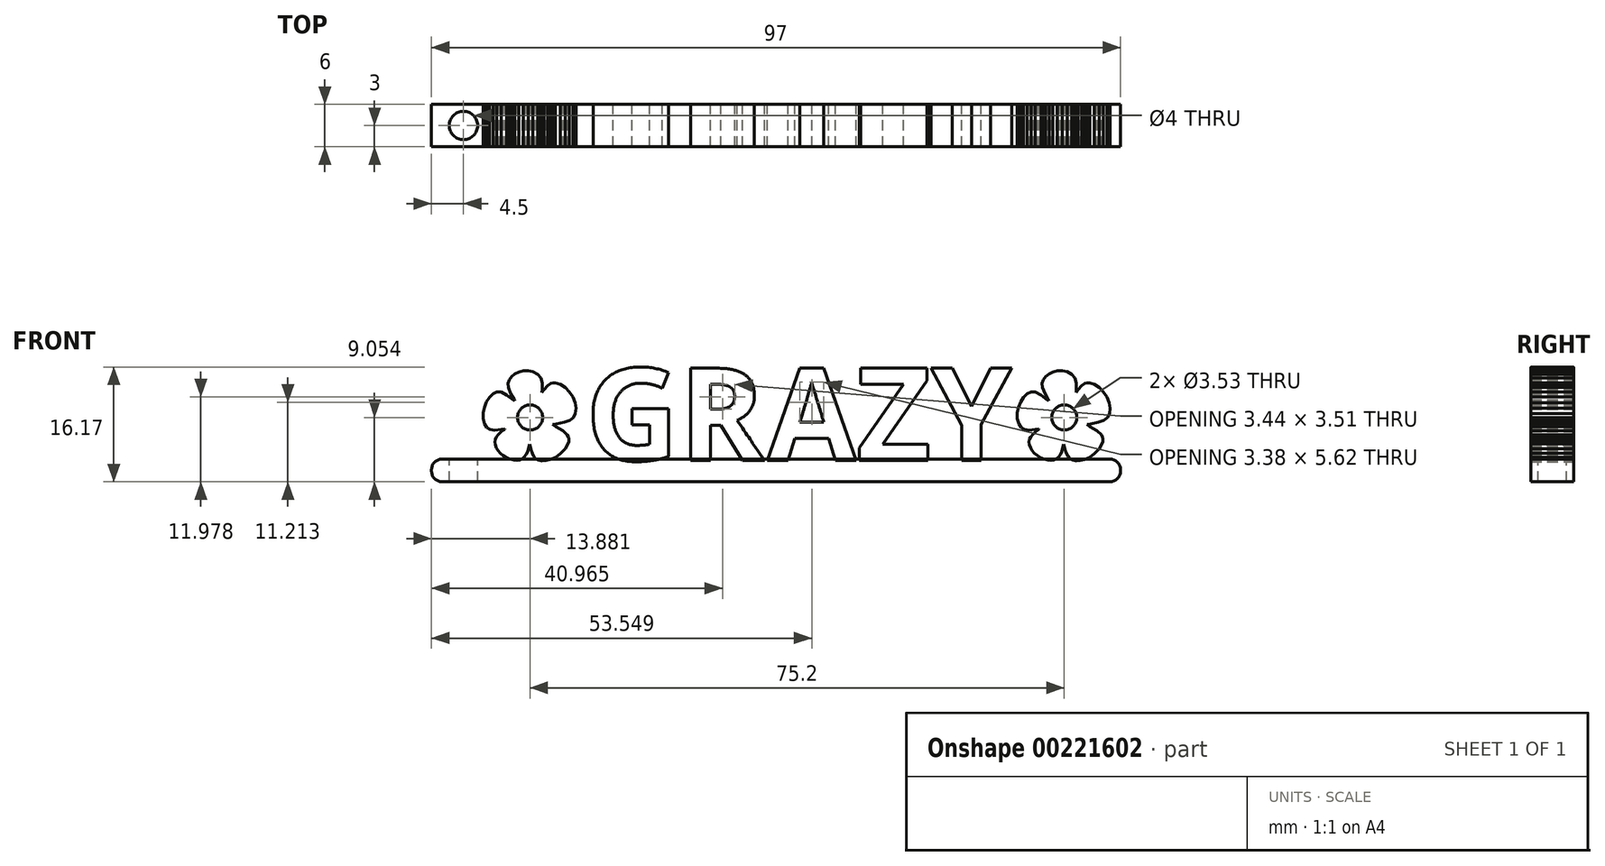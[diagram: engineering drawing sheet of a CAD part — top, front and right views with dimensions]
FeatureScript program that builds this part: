
annotation { "Feature Type Name" : "Feature", "Feature Type Description" : "" }
export const myFeature = defineFeature(function(context is Context, id is Id, definition is map)
    precondition{}
    {
        {
            var Q0;
            Q0=qCreatedBy(makeId("Front.planeOp"),FACE);
            var sketch = newSketch(context, id + "F0", { "sketchPlane" : qUnion([Q0])});
            skText(sketch, "E0", { "text": "   GRAZY", "fontName": "OpenSans-Bold.ttf"});
            skLineSegment(sketch, "E1.0.0", {"start": v(-9.3, 0.1) * mm, "end": v(-8.53, 0.46) * mm});
            skLineSegment(sketch, "E1.0.1", {"start": v(-8.53, 0.46) * mm, "end": v(-7.79, 1.02) * mm});
            skLineSegment(sketch, "E1.0.2", {"start": v(-7.79, 1.02) * mm, "end": v(-7.18, 1.67) * mm});
            skLineSegment(sketch, "E1.0.3", {"start": v(-7.18, 1.67) * mm, "end": v(-6.78, 2.35) * mm});
            skLineSegment(sketch, "E1.0.4", {"start": v(-6.78, 2.35) * mm, "end": v(-6.68, 2.7) * mm});
            skLineSegment(sketch, "E1.0.5", {"start": v(-6.68, 2.7) * mm, "end": v(-6.67, 3.02) * mm});
            skLineSegment(sketch, "E1.0.6", {"start": v(-6.67, 3.02) * mm, "end": v(-6.73, 3.33) * mm});
            skLineSegment(sketch, "E1.0.7", {"start": v(-6.73, 3.33) * mm, "end": v(-6.89, 3.62) * mm});
            skLineSegment(sketch, "E1.0.8", {"start": v(-6.89, 3.62) * mm, "end": v(-7.48, 4.2) * mm});
            skLineSegment(sketch, "E1.0.9", {"start": v(-7.48, 4.2) * mm, "end": v(-8.5, 4.79) * mm});
            skLineSegment(sketch, "E1.0.10", {"start": v(-8.5, 4.79) * mm, "end": v(-8.93, 5.06) * mm});
            skLineSegment(sketch, "E1.0.11", {"start": v(-8.93, 5.06) * mm, "end": v(-8.42, 5.16) * mm});
            skLineSegment(sketch, "E1.0.12", {"start": v(-8.42, 5.16) * mm, "end": v(-7.31, 5.37) * mm});
            skLineSegment(sketch, "E1.0.13", {"start": v(-7.31, 5.37) * mm, "end": v(-6.55, 5.65) * mm});
            skLineSegment(sketch, "E1.0.14", {"start": v(-6.55, 5.65) * mm, "end": v(-6.05, 6.04) * mm});
            skLineSegment(sketch, "E1.0.15", {"start": v(-6.05, 6.04) * mm, "end": v(-5.76, 6.58) * mm});
            skLineSegment(sketch, "E1.0.16", {"start": v(-5.76, 6.58) * mm, "end": v(-5.64, 7.33) * mm});
            skLineSegment(sketch, "E1.0.17", {"start": v(-5.64, 7.33) * mm, "end": v(-5.78, 8.14) * mm});
            skLineSegment(sketch, "E1.0.18", {"start": v(-5.78, 8.14) * mm, "end": v(-6.1, 8.93) * mm});
            skLineSegment(sketch, "E1.0.19", {"start": v(-6.1, 8.93) * mm, "end": v(-6.6, 9.67) * mm});
            skLineSegment(sketch, "E1.0.20", {"start": v(-6.6, 9.67) * mm, "end": v(-7.2, 10.28) * mm});
            skLineSegment(sketch, "E1.0.21", {"start": v(-7.2, 10.28) * mm, "end": v(-7.86, 10.72) * mm});
            skLineSegment(sketch, "E1.0.22", {"start": v(-7.86, 10.72) * mm, "end": v(-8.55, 10.93) * mm});
            skLineSegment(sketch, "E1.0.23", {"start": v(-8.55, 10.93) * mm, "end": v(-8.88, 10.93) * mm});
            skLineSegment(sketch, "E1.0.24", {"start": v(-8.88, 10.93) * mm, "end": v(-9.2, 10.85) * mm});
            skLineSegment(sketch, "E1.0.25", {"start": v(-9.2, 10.85) * mm, "end": v(-9.65, 10.56) * mm});
            skLineSegment(sketch, "E1.0.26", {"start": v(-9.65, 10.56) * mm, "end": v(-10.14, 9.98) * mm});
            skLineSegment(sketch, "E1.0.27", {"start": v(-10.14, 9.98) * mm, "end": v(-10.45, 9.58) * mm});
            skLineSegment(sketch, "E1.0.28", {"start": v(-10.45, 9.58) * mm, "end": v(-10.4, 10.03) * mm});
            skLineSegment(sketch, "E1.0.29", {"start": v(-10.4, 10.03) * mm, "end": v(-10.4, 10.93) * mm});
            skLineSegment(sketch, "E1.0.30", {"start": v(-10.4, 10.93) * mm, "end": v(-10.6, 11.63) * mm});
            skLineSegment(sketch, "E1.0.31", {"start": v(-10.6, 11.63) * mm, "end": v(-11.04, 12.15) * mm});
            skLineSegment(sketch, "E1.0.32", {"start": v(-11.04, 12.15) * mm, "end": v(-11.71, 12.5) * mm});
            skLineSegment(sketch, "E1.0.33", {"start": v(-11.71, 12.5) * mm, "end": v(-12.4, 12.64) * mm});
            skLineSegment(sketch, "E1.0.34", {"start": v(-12.4, 12.64) * mm, "end": v(-13.07, 12.62) * mm});
            skLineSegment(sketch, "E1.0.35", {"start": v(-13.07, 12.62) * mm, "end": v(-13.7, 12.47) * mm});
            skLineSegment(sketch, "E1.0.36", {"start": v(-13.7, 12.47) * mm, "end": v(-14.26, 12.2) * mm});
            skLineSegment(sketch, "E1.0.37", {"start": v(-14.26, 12.2) * mm, "end": v(-14.72, 11.83) * mm});
            skLineSegment(sketch, "E1.0.38", {"start": v(-14.72, 11.83) * mm, "end": v(-15.05, 11.38) * mm});
            skLineSegment(sketch, "E1.0.39", {"start": v(-15.05, 11.38) * mm, "end": v(-15.22, 10.87) * mm});
            skLineSegment(sketch, "E1.0.40", {"start": v(-15.22, 10.87) * mm, "end": v(-15.2, 10.3) * mm});
            skLineSegment(sketch, "E1.0.41", {"start": v(-15.2, 10.3) * mm, "end": v(-14.83, 9.4) * mm});
            skLineSegment(sketch, "E1.0.42", {"start": v(-14.83, 9.4) * mm, "end": v(-14.35, 8.55) * mm});
            skLineSegment(sketch, "E1.0.43", {"start": v(-14.35, 8.55) * mm, "end": v(-14.3, 8.4) * mm});
            skLineSegment(sketch, "E1.0.44", {"start": v(-14.3, 8.4) * mm, "end": v(-14.48, 8.53) * mm});
            skLineSegment(sketch, "E1.0.45", {"start": v(-14.48, 8.53) * mm, "end": v(-15.4, 9.23) * mm});
            skLineSegment(sketch, "E1.0.46", {"start": v(-15.4, 9.23) * mm, "end": v(-16.22, 9.63) * mm});
            skLineSegment(sketch, "E1.0.47", {"start": v(-16.22, 9.63) * mm, "end": v(-16.8, 9.63) * mm});
            skLineSegment(sketch, "E1.0.48", {"start": v(-16.8, 9.63) * mm, "end": v(-17.36, 9.37) * mm});
            skLineSegment(sketch, "E1.0.49", {"start": v(-17.36, 9.37) * mm, "end": v(-17.85, 8.9) * mm});
            skLineSegment(sketch, "E1.0.50", {"start": v(-17.85, 8.9) * mm, "end": v(-18.26, 8.26) * mm});
            skLineSegment(sketch, "E1.0.51", {"start": v(-18.26, 8.26) * mm, "end": v(-18.56, 7.51) * mm});
            skLineSegment(sketch, "E1.0.52", {"start": v(-18.56, 7.51) * mm, "end": v(-18.72, 6.71) * mm});
            skLineSegment(sketch, "E1.0.53", {"start": v(-18.72, 6.71) * mm, "end": v(-18.72, 5.9) * mm});
            skLineSegment(sketch, "E1.0.54", {"start": v(-18.72, 5.9) * mm, "end": v(-18.52, 5.16) * mm});
            skLineSegment(sketch, "E1.0.55", {"start": v(-18.52, 5.16) * mm, "end": v(-18.2, 4.64) * mm});
            skLineSegment(sketch, "E1.0.56", {"start": v(-18.2, 4.64) * mm, "end": v(-17.75, 4.36) * mm});
            skLineSegment(sketch, "E1.0.57", {"start": v(-17.75, 4.36) * mm, "end": v(-17.1, 4.27) * mm});
            skLineSegment(sketch, "E1.0.58", {"start": v(-17.1, 4.27) * mm, "end": v(-16.21, 4.37) * mm});
            skLineSegment(sketch, "E1.0.59", {"start": v(-16.21, 4.37) * mm, "end": v(-15.7, 4.43) * mm});
            skLineSegment(sketch, "E1.0.60", {"start": v(-15.7, 4.43) * mm, "end": v(-15.67, 4.4) * mm});
            skLineSegment(sketch, "E1.0.61", {"start": v(-15.67, 4.4) * mm, "end": v(-15.78, 4.33) * mm});
            skLineSegment(sketch, "E1.0.62", {"start": v(-15.78, 4.33) * mm, "end": v(-16.17, 4.07) * mm});
            skLineSegment(sketch, "E1.0.63", {"start": v(-16.17, 4.07) * mm, "end": v(-16.55, 3.71) * mm});
            skLineSegment(sketch, "E1.0.64", {"start": v(-16.55, 3.71) * mm, "end": v(-16.87, 3.33) * mm});
            skLineSegment(sketch, "E1.0.65", {"start": v(-16.87, 3.33) * mm, "end": v(-17.04, 3) * mm});
            skLineSegment(sketch, "E1.0.66", {"start": v(-17.04, 3) * mm, "end": v(-17.08, 2.6) * mm});
            skLineSegment(sketch, "E1.0.67", {"start": v(-17.08, 2.6) * mm, "end": v(-17.02, 2.2) * mm});
            skLineSegment(sketch, "E1.0.68", {"start": v(-17.02, 2.2) * mm, "end": v(-16.87, 1.78) * mm});
            skLineSegment(sketch, "E1.0.69", {"start": v(-16.87, 1.78) * mm, "end": v(-16.62, 1.39) * mm});
            skLineSegment(sketch, "E1.0.70", {"start": v(-16.62, 1.39) * mm, "end": v(-16.3, 1.02) * mm});
            skLineSegment(sketch, "E1.0.71", {"start": v(-16.3, 1.02) * mm, "end": v(-15.9, 0.69) * mm});
            skLineSegment(sketch, "E1.0.72", {"start": v(-15.9, 0.69) * mm, "end": v(-15.45, 0.4) * mm});
            skLineSegment(sketch, "E1.0.73", {"start": v(-15.45, 0.4) * mm, "end": v(-14.95, 0.2) * mm});
            skLineSegment(sketch, "E1.0.74", {"start": v(-14.95, 0.2) * mm, "end": v(-14.44, 0.06) * mm});
            skLineSegment(sketch, "E1.0.75", {"start": v(-14.44, 0.06) * mm, "end": v(-13.98, 0.02) * mm});
            skLineSegment(sketch, "E1.0.76", {"start": v(-13.98, 0.02) * mm, "end": v(-13.58, 0.08) * mm});
            skLineSegment(sketch, "E1.0.77", {"start": v(-13.58, 0.08) * mm, "end": v(-13.23, 0.23) * mm});
            skLineSegment(sketch, "E1.0.78", {"start": v(-13.23, 0.23) * mm, "end": v(-12.92, 0.49) * mm});
            skLineSegment(sketch, "E1.0.79", {"start": v(-12.92, 0.49) * mm, "end": v(-12.67, 0.84) * mm});
            skLineSegment(sketch, "E1.0.80", {"start": v(-12.67, 0.84) * mm, "end": v(-12.46, 1.28) * mm});
            skLineSegment(sketch, "E1.0.81", {"start": v(-12.46, 1.28) * mm, "end": v(-12.3, 1.83) * mm});
            skLineSegment(sketch, "E1.0.82", {"start": v(-12.3, 1.83) * mm, "end": v(-12.19, 2.26) * mm});
            skLineSegment(sketch, "E1.0.83", {"start": v(-12.19, 2.26) * mm, "end": v(-12.13, 2.1) * mm});
            skLineSegment(sketch, "E1.0.84", {"start": v(-12.13, 2.1) * mm, "end": v(-12.01, 1.53) * mm});
            skLineSegment(sketch, "E1.0.85", {"start": v(-12.01, 1.53) * mm, "end": v(-11.82, 1) * mm});
            skLineSegment(sketch, "E1.0.86", {"start": v(-11.82, 1) * mm, "end": v(-11.6, 0.55) * mm});
            skLineSegment(sketch, "E1.0.87", {"start": v(-11.6, 0.55) * mm, "end": v(-11.35, 0.26) * mm});
            skLineSegment(sketch, "E1.0.88", {"start": v(-11.35, 0.26) * mm, "end": v(-10.95, 0.05) * mm});
            skLineSegment(sketch, "E1.0.89", {"start": v(-10.95, 0.05) * mm, "end": v(-10.46, -0.04) * mm});
            skLineSegment(sketch, "E1.0.90", {"start": v(-10.46, -0.04) * mm, "end": v(-9.9, -0.03) * mm});
            skLineSegment(sketch, "E1.0.91", {"start": v(-9.9, -0.03) * mm, "end": v(-9.3, 0.1) * mm});
            skCircle(sketch, "E2", {"center": v(-12.12, 6.05) * mm, "radius": 1.77 * mm});
            skCircle(sketch, "E3.1.0.0", {"center": v(63.08, 6.05) * mm, "radius": 1.77 * mm});
            skLineSegment(sketch, "E3.1.0.1", {"start": v(64.75, 9.58) * mm, "end": v(64.8, 10.03) * mm});
            skLineSegment(sketch, "E3.1.0.2", {"start": v(68, 10.28) * mm, "end": v(67.34, 10.72) * mm});
            skLineSegment(sketch, "E3.1.0.3", {"start": v(56.48, 5.9) * mm, "end": v(56.68, 5.16) * mm});
            skLineSegment(sketch, "E3.1.0.4", {"start": v(60.94, 12.2) * mm, "end": v(60.48, 11.83) * mm});
            skLineSegment(sketch, "E3.1.0.5", {"start": v(58.9, 1.02) * mm, "end": v(59.3, 0.69) * mm});
            skLineSegment(sketch, "E3.1.0.6", {"start": v(58.98, 9.63) * mm, "end": v(58.4, 9.63) * mm});
            skLineSegment(sketch, "E3.1.0.7", {"start": v(56.64, 7.51) * mm, "end": v(56.48, 6.71) * mm});
            skLineSegment(sketch, "E3.1.0.8", {"start": v(59.8, 9.23) * mm, "end": v(58.98, 9.63) * mm});
            skLineSegment(sketch, "E3.1.0.9", {"start": v(58.4, 9.63) * mm, "end": v(57.84, 9.37) * mm});
            skLineSegment(sketch, "E3.1.0.10", {"start": v(65.06, 9.98) * mm, "end": v(64.75, 9.58) * mm});
            skLineSegment(sketch, "E3.1.0.11", {"start": v(64.6, 11.63) * mm, "end": v(64.16, 12.15) * mm});
            skLineSegment(sketch, "E3.1.0.12", {"start": v(64.16, 12.15) * mm, "end": v(63.49, 12.5) * mm});
            skLineSegment(sketch, "E3.1.0.13", {"start": v(64.8, 10.93) * mm, "end": v(64.6, 11.63) * mm});
            skLineSegment(sketch, "E3.1.0.14", {"start": v(59.75, 0.4) * mm, "end": v(60.25, 0.2) * mm});
            skLineSegment(sketch, "E3.1.0.15", {"start": v(65.3, -0.03) * mm, "end": v(65.9, 0.1) * mm});
            skLineSegment(sketch, "E3.1.0.16", {"start": v(56.48, 6.71) * mm, "end": v(56.48, 5.9) * mm});
            skLineSegment(sketch, "E3.1.0.17", {"start": v(65.9, 0.1) * mm, "end": v(66.67, 0.46) * mm});
            skLineSegment(sketch, "E3.1.0.18", {"start": v(59.3, 0.69) * mm, "end": v(59.75, 0.4) * mm});
            skLineSegment(sketch, "E3.1.0.19", {"start": v(56.68, 5.16) * mm, "end": v(57, 4.64) * mm});
            skLineSegment(sketch, "E3.1.0.20", {"start": v(67.89, 5.37) * mm, "end": v(68.65, 5.65) * mm});
            skLineSegment(sketch, "E3.1.0.21", {"start": v(66.67, 0.46) * mm, "end": v(67.41, 1.02) * mm});
            skLineSegment(sketch, "E3.1.0.22", {"start": v(68.6, 9.67) * mm, "end": v(68, 10.28) * mm});
            skLineSegment(sketch, "E3.1.0.23", {"start": v(64.8, 10.03) * mm, "end": v(64.8, 10.93) * mm});
            skLineSegment(sketch, "E3.1.0.24", {"start": v(57.84, 9.37) * mm, "end": v(57.35, 8.9) * mm});
            skLineSegment(sketch, "E3.1.0.25", {"start": v(63.49, 12.5) * mm, "end": v(62.8, 12.64) * mm});
            skLineSegment(sketch, "E3.1.0.26", {"start": v(62.13, 12.62) * mm, "end": v(61.5, 12.47) * mm});
            skLineSegment(sketch, "E3.1.0.27", {"start": v(68.02, 1.67) * mm, "end": v(68.42, 2.35) * mm});
            skLineSegment(sketch, "E3.1.0.28", {"start": v(69.1, 8.93) * mm, "end": v(68.6, 9.67) * mm});
            skLineSegment(sketch, "E3.1.0.29", {"start": v(62.8, 12.64) * mm, "end": v(62.13, 12.62) * mm});
            skLineSegment(sketch, "E3.1.0.30", {"start": v(67.41, 1.02) * mm, "end": v(68.02, 1.67) * mm});
            skLineSegment(sketch, "E3.1.0.31", {"start": v(57.35, 8.9) * mm, "end": v(56.94, 8.26) * mm});
            skLineSegment(sketch, "E3.1.0.32", {"start": v(56.94, 8.26) * mm, "end": v(56.64, 7.51) * mm});
            skLineSegment(sketch, "E3.1.0.33", {"start": v(61.5, 12.47) * mm, "end": v(60.94, 12.2) * mm});
            skLineSegment(sketch, "E3.1.0.34", {"start": v(68.42, 2.35) * mm, "end": v(68.52, 2.7) * mm});
            skLineSegment(sketch, "E3.1.0.35", {"start": v(58.4, 9.63) * mm, "end": v(57.84, 9.37) * mm});
            skLineSegment(sketch, "E3.1.0.36", {"start": v(62.8, 12.64) * mm, "end": v(62.13, 12.62) * mm});
            skLineSegment(sketch, "E3.1.0.37", {"start": v(67.89, 5.37) * mm, "end": v(68.65, 5.65) * mm});
            skLineSegment(sketch, "E3.1.0.38", {"start": v(64.25, 0.05) * mm, "end": v(64.74, -0.04) * mm});
            skLineSegment(sketch, "E3.1.0.39", {"start": v(69.1, 8.93) * mm, "end": v(68.6, 9.67) * mm});
            skLineSegment(sketch, "E3.1.0.40", {"start": v(65.3, -0.03) * mm, "end": v(65.9, 0.1) * mm});
            skLineSegment(sketch, "E3.1.0.41", {"start": v(65.06, 9.98) * mm, "end": v(64.75, 9.58) * mm});
            skLineSegment(sketch, "E3.1.0.42", {"start": v(67.41, 1.02) * mm, "end": v(68.02, 1.67) * mm});
            skLineSegment(sketch, "E3.1.0.43", {"start": v(68.42, 2.35) * mm, "end": v(68.52, 2.7) * mm});
            skLineSegment(sketch, "E3.1.0.44", {"start": v(56.48, 6.71) * mm, "end": v(56.48, 5.9) * mm});
            skLineSegment(sketch, "E3.1.0.45", {"start": v(65.9, 0.1) * mm, "end": v(66.67, 0.46) * mm});
            skLineSegment(sketch, "E3.1.0.46", {"start": v(62.13, 12.62) * mm, "end": v(61.5, 12.47) * mm});
            skLineSegment(sketch, "E3.1.0.47", {"start": v(60.94, 12.2) * mm, "end": v(60.48, 11.83) * mm});
            skLineSegment(sketch, "E3.1.0.48", {"start": v(59.75, 0.4) * mm, "end": v(60.25, 0.2) * mm});
            skLineSegment(sketch, "E3.1.0.49", {"start": v(64.8, 10.03) * mm, "end": v(64.8, 10.93) * mm});
            skLineSegment(sketch, "E3.1.0.50", {"start": v(64.75, 9.58) * mm, "end": v(64.8, 10.03) * mm});
            skLineSegment(sketch, "E3.1.0.51", {"start": v(64.74, -0.04) * mm, "end": v(65.3, -0.03) * mm});
            skLineSegment(sketch, "E3.1.0.52", {"start": v(58.98, 9.63) * mm, "end": v(58.4, 9.63) * mm});
            skLineSegment(sketch, "E3.1.0.53", {"start": v(64.8, 10.93) * mm, "end": v(64.6, 11.63) * mm});
            skLineSegment(sketch, "E3.1.0.54", {"start": v(68, 10.28) * mm, "end": v(67.34, 10.72) * mm});
            skLineSegment(sketch, "E3.1.0.55", {"start": v(57.35, 8.9) * mm, "end": v(56.94, 8.26) * mm});
            skLineSegment(sketch, "E3.1.0.56", {"start": v(59.3, 0.69) * mm, "end": v(59.75, 0.4) * mm});
            skLineSegment(sketch, "E3.1.0.57", {"start": v(63.49, 12.5) * mm, "end": v(62.8, 12.64) * mm});
            skLineSegment(sketch, "E3.1.0.58", {"start": v(57.84, 9.37) * mm, "end": v(57.35, 8.9) * mm});
            skLineSegment(sketch, "E3.1.0.59", {"start": v(56.48, 5.9) * mm, "end": v(56.68, 5.16) * mm});
            skLineSegment(sketch, "E3.1.0.60", {"start": v(64.16, 12.15) * mm, "end": v(63.49, 12.5) * mm});
            skLineSegment(sketch, "E3.1.0.61", {"start": v(59.8, 9.23) * mm, "end": v(58.98, 9.63) * mm});
            skLineSegment(sketch, "E3.1.0.62", {"start": v(66.67, 0.46) * mm, "end": v(67.41, 1.02) * mm});
            skLineSegment(sketch, "E3.1.0.63", {"start": v(64.6, 11.63) * mm, "end": v(64.16, 12.15) * mm});
            skLineSegment(sketch, "E3.1.0.64", {"start": v(56.94, 8.26) * mm, "end": v(56.64, 7.51) * mm});
            skLineSegment(sketch, "E3.1.0.65", {"start": v(68.02, 1.67) * mm, "end": v(68.42, 2.35) * mm});
            skLineSegment(sketch, "E3.1.0.66", {"start": v(56.64, 7.51) * mm, "end": v(56.48, 6.71) * mm});
            skLineSegment(sketch, "E3.1.0.67", {"start": v(58.9, 1.02) * mm, "end": v(59.3, 0.69) * mm});
            skLineSegment(sketch, "E3.1.0.68", {"start": v(56.68, 5.16) * mm, "end": v(57, 4.64) * mm});
            skLineSegment(sketch, "E3.1.0.69", {"start": v(61.5, 12.47) * mm, "end": v(60.94, 12.2) * mm});
            skLineSegment(sketch, "E3.1.0.70", {"start": v(68.6, 9.67) * mm, "end": v(68, 10.28) * mm});
            skLineSegment(sketch, "E3.1.0.71", {"start": v(60.48, 11.83) * mm, "end": v(60.15, 11.38) * mm});
            skLineSegment(sketch, "E3.1.0.72", {"start": v(67.34, 10.72) * mm, "end": v(66.65, 10.93) * mm});
            skLineSegment(sketch, "E3.1.0.73", {"start": v(69.15, 6.04) * mm, "end": v(69.44, 6.58) * mm});
            skLineSegment(sketch, "E3.1.0.74", {"start": v(68.52, 2.7) * mm, "end": v(68.53, 3.02) * mm});
            skLineSegment(sketch, "E3.1.0.75", {"start": v(66.65, 10.93) * mm, "end": v(66.32, 10.93) * mm});
            skLineSegment(sketch, "E3.1.0.76", {"start": v(57, 4.64) * mm, "end": v(57.45, 4.36) * mm});
            skLineSegment(sketch, "E3.1.0.77", {"start": v(66, 10.85) * mm, "end": v(65.55, 10.56) * mm});
            skLineSegment(sketch, "E3.1.0.78", {"start": v(66.78, 5.16) * mm, "end": v(67.89, 5.37) * mm});
            skLineSegment(sketch, "E3.1.0.79", {"start": v(68.53, 3.02) * mm, "end": v(68.47, 3.33) * mm});
            skLineSegment(sketch, "E3.1.0.80", {"start": v(68.47, 3.33) * mm, "end": v(68.31, 3.62) * mm});
            skLineSegment(sketch, "E3.1.0.81", {"start": v(67.72, 4.2) * mm, "end": v(66.7, 4.79) * mm});
            skLineSegment(sketch, "E3.1.0.82", {"start": v(69.56, 7.33) * mm, "end": v(69.42, 8.14) * mm});
            skLineSegment(sketch, "E3.1.0.83", {"start": v(58.58, 1.39) * mm, "end": v(58.9, 1.02) * mm});
            skLineSegment(sketch, "E3.1.0.84", {"start": v(60.76, 0.06) * mm, "end": v(61.22, 0.02) * mm});
            skLineSegment(sketch, "E3.1.0.85", {"start": v(66.27, 5.06) * mm, "end": v(66.78, 5.16) * mm});
            skLineSegment(sketch, "E3.1.0.86", {"start": v(63.85, 0.26) * mm, "end": v(64.25, 0.05) * mm});
            skLineSegment(sketch, "E3.1.0.87", {"start": v(60.15, 11.38) * mm, "end": v(59.98, 10.87) * mm});
            skLineSegment(sketch, "E3.1.0.88", {"start": v(69.44, 6.58) * mm, "end": v(69.56, 7.33) * mm});
            skLineSegment(sketch, "E3.1.0.89", {"start": v(64.25, 0.05) * mm, "end": v(64.74, -0.04) * mm});
            skLineSegment(sketch, "E3.1.0.90", {"start": v(66.7, 4.79) * mm, "end": v(66.27, 5.06) * mm});
            skLineSegment(sketch, "E3.1.0.91", {"start": v(60.25, 0.2) * mm, "end": v(60.76, 0.06) * mm});
            skLineSegment(sketch, "E3.1.0.92", {"start": v(60, 10.3) * mm, "end": v(60.37, 9.4) * mm});
            skLineSegment(sketch, "E3.1.0.93", {"start": v(58.33, 1.78) * mm, "end": v(58.58, 1.39) * mm});
            skLineSegment(sketch, "E3.1.0.94", {"start": v(68.31, 3.62) * mm, "end": v(67.72, 4.2) * mm});
            skLineSegment(sketch, "E3.1.0.95", {"start": v(64.74, -0.04) * mm, "end": v(65.3, -0.03) * mm});
            skLineSegment(sketch, "E3.1.0.96", {"start": v(59.98, 10.87) * mm, "end": v(60, 10.3) * mm});
            skLineSegment(sketch, "E3.1.0.97", {"start": v(68.65, 5.65) * mm, "end": v(69.15, 6.04) * mm});
            skLineSegment(sketch, "E3.1.0.98", {"start": v(66.32, 10.93) * mm, "end": v(66, 10.85) * mm});
            skLineSegment(sketch, "E3.1.0.99", {"start": v(65.55, 10.56) * mm, "end": v(65.06, 9.98) * mm});
            skLineSegment(sketch, "E3.1.0.100", {"start": v(61.22, 0.02) * mm, "end": v(61.62, 0.08) * mm});
            skLineSegment(sketch, "E3.1.0.101", {"start": v(58.18, 2.2) * mm, "end": v(58.33, 1.78) * mm});
            skLineSegment(sketch, "E3.1.0.102", {"start": v(69.42, 8.14) * mm, "end": v(69.1, 8.93) * mm});
            skLineSegment(sketch, "E3.1.0.103", {"start": v(66.7, 4.79) * mm, "end": v(66.27, 5.06) * mm});
            skLineSegment(sketch, "E3.1.0.104", {"start": v(66.27, 5.06) * mm, "end": v(66.78, 5.16) * mm});
            skLineSegment(sketch, "E3.1.0.105", {"start": v(57, 4.64) * mm, "end": v(57.45, 4.36) * mm});
            skLineSegment(sketch, "E3.1.0.106", {"start": v(63.6, 0.55) * mm, "end": v(63.85, 0.26) * mm});
            skLineSegment(sketch, "E3.1.0.107", {"start": v(63.85, 0.26) * mm, "end": v(64.25, 0.05) * mm});
            skLineSegment(sketch, "E3.1.0.108", {"start": v(58.33, 1.78) * mm, "end": v(58.58, 1.39) * mm});
            skLineSegment(sketch, "E3.1.0.109", {"start": v(68.31, 3.62) * mm, "end": v(67.72, 4.2) * mm});
            skLineSegment(sketch, "E3.1.0.110", {"start": v(66.78, 5.16) * mm, "end": v(67.89, 5.37) * mm});
            skLineSegment(sketch, "E3.1.0.111", {"start": v(60, 10.3) * mm, "end": v(60.37, 9.4) * mm});
            skLineSegment(sketch, "E3.1.0.112", {"start": v(68.65, 5.65) * mm, "end": v(69.15, 6.04) * mm});
            skLineSegment(sketch, "E3.1.0.113", {"start": v(65.55, 10.56) * mm, "end": v(65.06, 9.98) * mm});
            skLineSegment(sketch, "E3.1.0.114", {"start": v(69.44, 6.58) * mm, "end": v(69.56, 7.33) * mm});
            skLineSegment(sketch, "E3.1.0.115", {"start": v(59.98, 10.87) * mm, "end": v(60, 10.3) * mm});
            skLineSegment(sketch, "E3.1.0.116", {"start": v(66.32, 10.93) * mm, "end": v(66, 10.85) * mm});
            skLineSegment(sketch, "E3.1.0.117", {"start": v(61.22, 0.02) * mm, "end": v(61.62, 0.08) * mm});
            skLineSegment(sketch, "E3.1.0.118", {"start": v(66, 10.85) * mm, "end": v(65.55, 10.56) * mm});
            skLineSegment(sketch, "E3.1.0.119", {"start": v(60.76, 0.06) * mm, "end": v(61.22, 0.02) * mm});
            skLineSegment(sketch, "E3.1.0.120", {"start": v(60.25, 0.2) * mm, "end": v(60.76, 0.06) * mm});
            skLineSegment(sketch, "E3.1.0.121", {"start": v(67.72, 4.2) * mm, "end": v(66.7, 4.79) * mm});
            skLineSegment(sketch, "E3.1.0.122", {"start": v(69.15, 6.04) * mm, "end": v(69.44, 6.58) * mm});
            skLineSegment(sketch, "E3.1.0.123", {"start": v(58.12, 2.6) * mm, "end": v(58.18, 2.2) * mm});
            skLineSegment(sketch, "E3.1.0.124", {"start": v(68.52, 2.7) * mm, "end": v(68.53, 3.02) * mm});
            skLineSegment(sketch, "E3.1.0.125", {"start": v(58.58, 1.39) * mm, "end": v(58.9, 1.02) * mm});
            skLineSegment(sketch, "E3.1.0.126", {"start": v(69.42, 8.14) * mm, "end": v(69.1, 8.93) * mm});
            skLineSegment(sketch, "E3.1.0.127", {"start": v(69.56, 7.33) * mm, "end": v(69.42, 8.14) * mm});
            skLineSegment(sketch, "E3.1.0.128", {"start": v(68.53, 3.02) * mm, "end": v(68.47, 3.33) * mm});
            skLineSegment(sketch, "E3.1.0.129", {"start": v(58.18, 2.2) * mm, "end": v(58.33, 1.78) * mm});
            skLineSegment(sketch, "E3.1.0.130", {"start": v(68.47, 3.33) * mm, "end": v(68.31, 3.62) * mm});
            skLineSegment(sketch, "E3.1.0.131", {"start": v(60.15, 11.38) * mm, "end": v(59.98, 10.87) * mm});
            skLineSegment(sketch, "E3.1.0.132", {"start": v(66.65, 10.93) * mm, "end": v(66.32, 10.93) * mm});
            skLineSegment(sketch, "E3.1.0.133", {"start": v(67.34, 10.72) * mm, "end": v(66.65, 10.93) * mm});
            skLineSegment(sketch, "E3.1.0.134", {"start": v(60.48, 11.83) * mm, "end": v(60.15, 11.38) * mm});
            skLineSegment(sketch, "E3.1.0.135", {"start": v(58.12, 2.6) * mm, "end": v(58.18, 2.2) * mm});
            skLineSegment(sketch, "E3.1.0.136", {"start": v(58.99, 4.37) * mm, "end": v(59.5, 4.43) * mm});
            skLineSegment(sketch, "E3.1.0.137", {"start": v(63.19, 1.53) * mm, "end": v(63.38, 1) * mm});
            skLineSegment(sketch, "E3.1.0.138", {"start": v(59.42, 4.33) * mm, "end": v(59.03, 4.07) * mm});
            skLineSegment(sketch, "E3.1.0.139", {"start": v(61.97, 0.23) * mm, "end": v(62.28, 0.49) * mm});
            skLineSegment(sketch, "E3.1.0.140", {"start": v(62.53, 0.84) * mm, "end": v(62.74, 1.28) * mm});
            skLineSegment(sketch, "E3.1.0.141", {"start": v(63.38, 1) * mm, "end": v(63.6, 0.55) * mm});
            skLineSegment(sketch, "E3.1.0.142", {"start": v(59.03, 4.07) * mm, "end": v(58.65, 3.71) * mm});
            skLineSegment(sketch, "E3.1.0.143", {"start": v(63.07, 2.1) * mm, "end": v(63.19, 1.53) * mm});
            skLineSegment(sketch, "E3.1.0.144", {"start": v(62.28, 0.49) * mm, "end": v(62.53, 0.84) * mm});
            skLineSegment(sketch, "E3.1.0.145", {"start": v(58.1, 4.27) * mm, "end": v(58.99, 4.37) * mm});
            skLineSegment(sketch, "E3.1.0.146", {"start": v(58.65, 3.71) * mm, "end": v(58.33, 3.33) * mm});
            skLineSegment(sketch, "E3.1.0.147", {"start": v(57.45, 4.36) * mm, "end": v(58.1, 4.27) * mm});
            skLineSegment(sketch, "E3.1.0.148", {"start": v(62.74, 1.28) * mm, "end": v(62.9, 1.83) * mm});
            skLineSegment(sketch, "E3.1.0.149", {"start": v(63.01, 2.26) * mm, "end": v(63.07, 2.1) * mm});
            skLineSegment(sketch, "E3.1.0.150", {"start": v(58.33, 3.33) * mm, "end": v(58.16, 3) * mm});
            skLineSegment(sketch, "E3.1.0.151", {"start": v(63.6, 0.55) * mm, "end": v(63.85, 0.26) * mm});
            skLineSegment(sketch, "E3.1.0.152", {"start": v(62.9, 1.83) * mm, "end": v(63.01, 2.26) * mm});
            skLineSegment(sketch, "E3.1.0.153", {"start": v(58.16, 3) * mm, "end": v(58.12, 2.6) * mm});
            skLineSegment(sketch, "E3.1.0.154", {"start": v(61.62, 0.08) * mm, "end": v(61.97, 0.23) * mm});
            skLineSegment(sketch, "E3.1.0.155", {"start": v(59.53, 4.4) * mm, "end": v(59.42, 4.33) * mm});
            skLineSegment(sketch, "E3.1.0.156", {"start": v(63.01, 2.26) * mm, "end": v(63.07, 2.1) * mm});
            skLineSegment(sketch, "E3.1.0.157", {"start": v(58.1, 4.27) * mm, "end": v(58.99, 4.37) * mm});
            skLineSegment(sketch, "E3.1.0.158", {"start": v(63.19, 1.53) * mm, "end": v(63.38, 1) * mm});
            skLineSegment(sketch, "E3.1.0.159", {"start": v(59.5, 4.43) * mm, "end": v(59.53, 4.4) * mm});
            skLineSegment(sketch, "E3.1.0.160", {"start": v(58.65, 3.71) * mm, "end": v(58.33, 3.33) * mm});
            skLineSegment(sketch, "E3.1.0.161", {"start": v(57.45, 4.36) * mm, "end": v(58.1, 4.27) * mm});
            skLineSegment(sketch, "E3.1.0.162", {"start": v(58.99, 4.37) * mm, "end": v(59.5, 4.43) * mm});
            skLineSegment(sketch, "E3.1.0.163", {"start": v(61.62, 0.08) * mm, "end": v(61.97, 0.23) * mm});
            skLineSegment(sketch, "E3.1.0.164", {"start": v(59.03, 4.07) * mm, "end": v(58.65, 3.71) * mm});
            skLineSegment(sketch, "E3.1.0.165", {"start": v(63.07, 2.1) * mm, "end": v(63.19, 1.53) * mm});
            skLineSegment(sketch, "E3.1.0.166", {"start": v(62.9, 1.83) * mm, "end": v(63.01, 2.26) * mm});
            skLineSegment(sketch, "E3.1.0.167", {"start": v(59.42, 4.33) * mm, "end": v(59.03, 4.07) * mm});
            skLineSegment(sketch, "E3.1.0.168", {"start": v(61.97, 0.23) * mm, "end": v(62.28, 0.49) * mm});
            skLineSegment(sketch, "E3.1.0.169", {"start": v(58.16, 3) * mm, "end": v(58.12, 2.6) * mm});
            skLineSegment(sketch, "E3.1.0.170", {"start": v(63.38, 1) * mm, "end": v(63.6, 0.55) * mm});
            skLineSegment(sketch, "E3.1.0.171", {"start": v(62.28, 0.49) * mm, "end": v(62.53, 0.84) * mm});
            skLineSegment(sketch, "E3.1.0.172", {"start": v(62.53, 0.84) * mm, "end": v(62.74, 1.28) * mm});
            skLineSegment(sketch, "E3.1.0.173", {"start": v(58.33, 3.33) * mm, "end": v(58.16, 3) * mm});
            skLineSegment(sketch, "E3.1.0.174", {"start": v(62.74, 1.28) * mm, "end": v(62.9, 1.83) * mm});
            skLineSegment(sketch, "E3.1.0.175", {"start": v(59.53, 4.4) * mm, "end": v(59.42, 4.33) * mm});
            skLineSegment(sketch, "E3.1.0.176", {"start": v(59.5, 4.43) * mm, "end": v(59.53, 4.4) * mm});
            skLineSegment(sketch, "E3.1.0.177", {"start": v(60.9, 8.4) * mm, "end": v(60.72, 8.53) * mm});
            skLineSegment(sketch, "E3.1.0.178", {"start": v(60.85, 8.55) * mm, "end": v(60.9, 8.4) * mm});
            skLineSegment(sketch, "E3.1.0.179", {"start": v(60.37, 9.4) * mm, "end": v(60.85, 8.55) * mm});
            skLineSegment(sketch, "E3.1.0.180", {"start": v(60.72, 8.53) * mm, "end": v(59.8, 9.23) * mm});
            skLineSegment(sketch, "E3.1.0.181", {"start": v(60.85, 8.55) * mm, "end": v(60.9, 8.4) * mm});
            skLineSegment(sketch, "E3.1.0.182", {"start": v(60.37, 9.4) * mm, "end": v(60.85, 8.55) * mm});
            skLineSegment(sketch, "E3.1.0.183", {"start": v(60.72, 8.53) * mm, "end": v(59.8, 9.23) * mm});
            skLineSegment(sketch, "E3.1.0.184", {"start": v(60.9, 8.4) * mm, "end": v(60.72, 8.53) * mm});
            skLineSegment(sketch, "E3.direction1", {"start": v(-16.3, 1.02) * mm, "end": v(42.4, 1.02) * mm, "construction": true});
            const initialGuessF0  = {"E0": [-0.0185, 0, 1, 0, 0.0131]};
            skSetInitialGuess(sketch, initialGuessF0);
            skSolve(sketch);
        }
        {
            var Q0;
            Q0=qSketchRegion(id+"F0",true);
            extrude(context, id + "F1", {"entities" : qUnion([Q0]), "endBound" : BoundingType.SYMMETRIC, "depth" : 6 * mm});
        }
        {
            var Q0;
            Q0=qCreatedBy(makeId("Top.planeOp"),FACE);
            var sketch = newSketch(context, id + "F2", { "sketchPlane" : qUnion([Q0])});
            skLineSegment(sketch, "E4.bottom", {"start": v(-18.5, 3) * mm, "end": v(71, 3) * mm});
            skLineSegment(sketch, "E4.top", {"start": v(-18.5, -3) * mm, "end": v(71, -3) * mm});
            skLineSegment(sketch, "E4.left", {"start": v(-18.5, 3) * mm, "end": v(-18.5, -3) * mm});
            skLineSegment(sketch, "E4.right", {"start": v(71, 3) * mm, "end": v(71, -3) * mm});
            skSolve(sketch);
        }
        {
            var Q0;
            Q0=makeQuery(id+"F2.imprint","IMPRINT",FACE,{"disambiguationData":[TD([[makeQuery(id+"F2.imprint","IMPRINT",EDGE,{"derivedFrom":sQuery(id+"F2.wireOp",EDGE,"E4.bottom")}),-1.0]])]});
            extrude(context, id + "F3", {"entities" : qUnion([Q0]), "depth" : 0.2 * mm});
        }
        {
            var Q0;
            Q0=makeQuery(id+"F3.opExtrude","CAP_FACE",FACE,{"disambiguationData":[OSD([sQuery(id+"F2.wireOp",EDGE,"E4.bottom"),sQuery(id+"F2.wireOp",EDGE,"E4.top"),sQuery(id+"F2.wireOp",EDGE,"E4.left"),sQuery(id+"F2.wireOp",EDGE,"E4.right")])],"isStart":true});
            extrude(context, id + "F4", {"entities" : qUnion([Q0]), "depth" : 3 * mm});
        }
        {
            var Q0;
            {var subQ0=sQuery(id+"F2.wireOp",EDGE,"E4.left");Q0=makeQuery(id+"FaVoHrOpcFZXiYX_6.opBoolean","MERGE",FACE,{"derivedFrom":[makeQuery(id+"F3.opExtrude","SWEPT_FACE",FACE,{"disambiguationData":[OSD([subQ0])]}),makeQuery(id+"F4.opExtrude","SWEPT_FACE",FACE,{"disambiguationData":[OSD([subQ0])]})]});}
            var sketch = newSketch(context, id + "F5", { "sketchPlane" : qUnion([Q0])});
            skLineSegment(sketch, "E5.bottom", {"start": v(-3, -3) * mm, "end": v(3, -3) * mm});
            skLineSegment(sketch, "E5.top", {"start": v(-3, 0.2) * mm, "end": v(3, 0.2) * mm});
            skLineSegment(sketch, "E5.left", {"start": v(-3, -3) * mm, "end": v(-3, 0.2) * mm});
            skLineSegment(sketch, "E5.right", {"start": v(3, -3) * mm, "end": v(3, 0.2) * mm});
            skSolve(sketch);
        }
        {
            var Q0;
            Q0=qSketchRegion(id+"F5",true);
            extrude(context, id + "F6", {"entities" : qUnion([Q0]), "operationType" : NewBodyOperationType.ADD, "depth" : 7.5 * mm});
        }
        {
            var Q0;
            Q0=makeQuery(id+"F6.opExtrude","CAP_EDGE",EDGE,{"disambiguationData":[OSD([sQuery(id+"F5.wireOp",EDGE,"E5.bottom")])],"isStart":false});
            var Q1;
            Q1=makeQuery(id+"F6.opExtrude","CAP_EDGE",EDGE,{"disambiguationData":[OSD([sQuery(id+"F5.wireOp",EDGE,"E5.top")])],"isStart":false});
            var Q2;
            Q2=makeQuery(id+"F4.opExtrude","CAP_EDGE",EDGE,{"disambiguationData":[OSD([sQuery(id+"F2.wireOp",EDGE,"E4.right")])],"isStart":false});
            fillet(context, id + "F7", {"entities" : qUnion([Q0, Q1, Q2]), "radius" : 1.5 * mm, "tangentPropagation" : true, "allowEdgeOverflow" : false});
        }
        {
            var Q0;
            {var subQ19=sQuery(id+"F2.wireOp",EDGE,"E4.top");var subQ20=sQuery(id+"F2.wireOp",EDGE,"E4.bottom");var subQ63=sQuery(id+"F0.wireOp",EDGE,"E0.sketch_text.stroke-2");var subQ66=sQuery(id+"F2.wireOp",EDGE,"E4.left");Q0=makeQuery(id+"F6.boolean.opBoolean","MERGE",FACE,{"derivedFrom":[makeQuery(id+"FaVoHrOpcFZXiYX_6.opBoolean","SPLIT",FACE,{"disambiguationData":[TD([makeQuery(id+"F1.opExtrude","SWEPT_FACE",FACE,{"disambiguationData":[OSD([subQ63])]})])],"derivedFrom":makeQuery(id+"F3.opExtrude","CAP_FACE",FACE,{"disambiguationData":[OSD([subQ20,subQ19,subQ66,sQuery(id+"F2.wireOp",EDGE,"E4.right")])],"isStart":false})}),makeQuery(id+"F6.opExtrude","SWEPT_FACE",FACE,{"disambiguationData":[OSD([sQuery(id+"F5.wireOp",EDGE,"E5.top")])]})]});}
            var sketch = newSketch(context, id + "F8", { "sketchPlane" : qUnion([Q0])});
            skCircle(sketch, "E6", {"center": v(-21.5, 0) * mm, "radius": 2 * mm});
            skSolve(sketch);
        }
        {
            var Q0;
            Q0=makeQuery(id+"F8.imprint","IMPRINT",FACE,{"disambiguationData":[TD([[makeQuery(id+"F8.imprint","IMPRINT",EDGE,{"derivedFrom":sQuery(id+"F8.wireOp",EDGE,"E6")}),1.0]])]});
            extrude(context, id + "F9", {"entities" : qUnion([Q0]), "operationType" : NewBodyOperationType.REMOVE, "oppositeDirection" : true, "depth" : 4 * mm});
        }
        {
            var Q0;
            Q0=makeQuery(id+"F3.opExtrude","CAP_EDGE",EDGE,{"disambiguationData":[OSD([sQuery(id+"F2.wireOp",EDGE,"E4.right")])],"isStart":false});
            fillet(context, id + "F10", {"entities" : qUnion([Q0]), "radius" : 1.5 * mm, "tangentPropagation" : true, "allowEdgeOverflow" : false});
        }
    });
